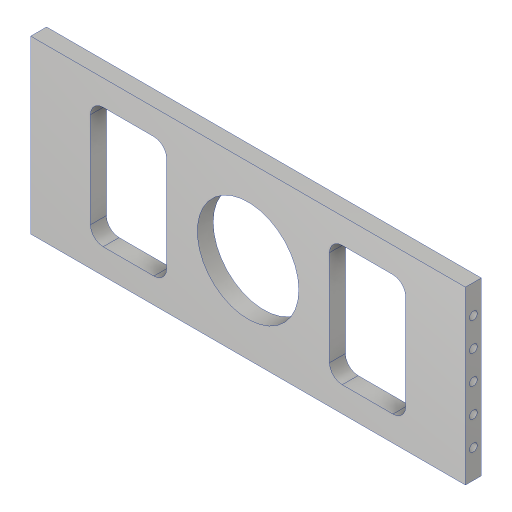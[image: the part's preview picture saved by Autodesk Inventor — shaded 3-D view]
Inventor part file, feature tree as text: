
AUTODESK INVENTOR PART (.ipt)
format: ipt  version: 2023.2 (Build 272271000, 271)  size: 204,800 bytes
history: native  units: mm
features: extrude x5, sketch x4, projected_geometry x3, other x1
ambient origin geometry x8: Origin, YZ Plane, XZ Plane, XY Plane, X Axis, Y Axis, Z Axis, Center Point
bodies: Body1 (feature_tree)
feature tree (13):
  other  "솔리드1"
  extrude  "돌출1"  Depth=137.0mm
  extrude  "돌출2"  Depth=54.0mm
  extrude  "돌출3"  Depth=27.0mm
  extrude  "돌출4"  Depth=68.5mm
  extrude  "돌출8"  Depth=5.0mm TaperAngle=0.0deg
  sketch  "스케치1"
  sketch  "스케치2"
  projected_geometry  "투영된 루프1"
  sketch  "스케치3"
  projected_geometry  "투영된 루프2"
  projected_geometry  "투영된 루프3"
  sketch  "스케치9"
